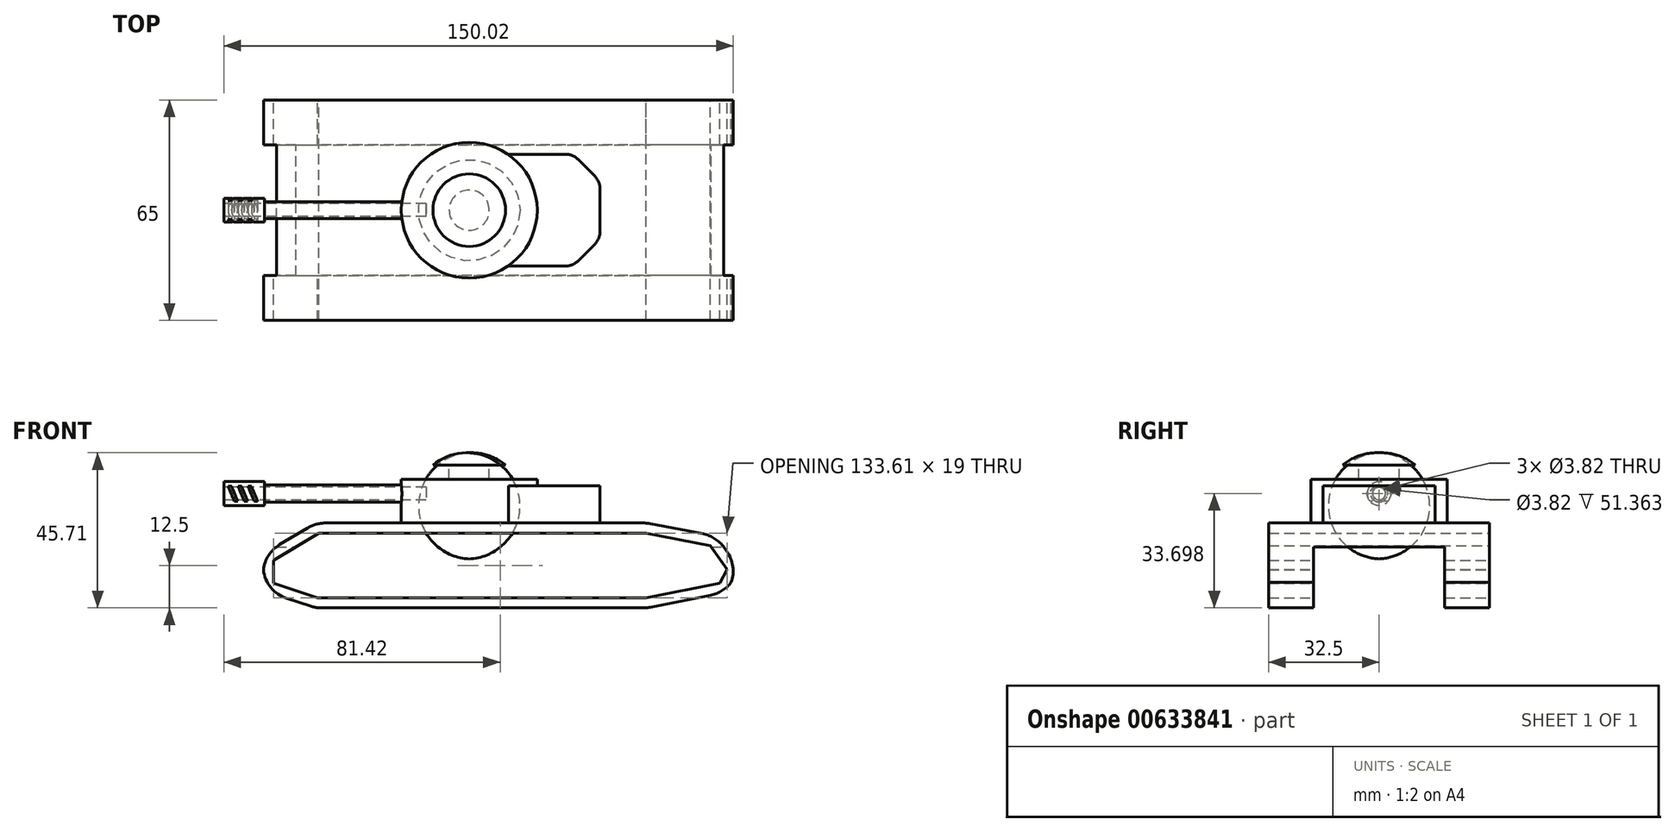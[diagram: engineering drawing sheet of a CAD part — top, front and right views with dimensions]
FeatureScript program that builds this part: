
annotation { "Feature Type Name" : "Feature", "Feature Type Description" : "" }
export const myFeature = defineFeature(function(context is Context, id is Id, definition is map)
    precondition{}
    {
        {
            var Q0;
            Q0=qCreatedBy(makeId("Front.planeOp"),FACE);
            var sketch = newSketch(context, id + "F0", { "sketchPlane" : qUnion([Q0])});
            skLineSegment(sketch, "E0.bottom", {"start": v(0, 0) * mm, "end": v(52.39, 0) * mm});
            skLineSegment(sketch, "E0.top", {"start": v(0, 25) * mm, "end": v(52.39, 25) * mm});
            skLineSegment(sketch, "E1.bottom", {"start": v(0, 25) * mm, "end": v(-45.2, 25) * mm});
            skLineSegment(sketch, "E1.top", {"start": v(0, 0) * mm, "end": v(-45.2, 0) * mm});
            skLineSegment(sketch, "E2", {"start": v(-45.2, 25) * mm, "end": v(-60.69, 15.75) * mm});
            skLineSegment(sketch, "E3", {"start": v(-60.69, 15.75) * mm, "end": v(-60.69, 5.11) * mm});
            skLineSegment(sketch, "E4", {"start": v(-60.69, 5.11) * mm, "end": v(-45.2, 0) * mm});
            skLineSegment(sketch, "E5", {"start": v(52.39, 25) * mm, "end": v(72.74, 21.07) * mm});
            skLineSegment(sketch, "E6", {"start": v(72.74, 21.07) * mm, "end": v(79.44, 11.59) * mm});
            skLineSegment(sketch, "E7", {"start": v(79.44, 11.59) * mm, "end": v(75.74, 4.65) * mm});
            skLineSegment(sketch, "E8", {"start": v(75.74, 4.65) * mm, "end": v(52.39, 0) * mm});
            skLineSegment(sketch, "E9.bottom", {"start": v(20.02, 37.95) * mm, "end": v(-20.02, 37.95) * mm});
            skLineSegment(sketch, "E9.left", {"start": v(20.02, 37.95) * mm, "end": v(20.02, 25) * mm});
            skLineSegment(sketch, "E9.right", {"start": v(-20.02, 37.95) * mm, "end": v(-20.02, 25) * mm});
            skPoint(sketch, "E9.middle", {"position": v(0, 25) * mm});
            skLineSegment(sketch, "E10", {"start": v(0, 37.95) * mm, "end": v(0, 25) * mm});
            skLineSegment(sketch, "E11.bottom", {"start": v(5.91, 42.11) * mm, "end": v(-5.91, 42.11) * mm});
            skLineSegment(sketch, "E11.top", {"start": v(5.91, 33.79) * mm, "end": v(-5.91, 33.79) * mm});
            skLineSegment(sketch, "E11.left", {"start": v(5.91, 42.11) * mm, "end": v(5.91, 33.79) * mm});
            skLineSegment(sketch, "E11.right", {"start": v(-5.91, 42.11) * mm, "end": v(-5.91, 33.79) * mm});
            skPoint(sketch, "E11.middle", {"position": v(0, 37.95) * mm});
            skArc(sketch, "E12", {"start": v(10.7, 42.11) * mm, "mid": v(5.68, 44.9) * mm, "end": v(0, 45.7) * mm});
            skLineSegment(sketch, "E13", {"start": v(5.91, 42.11) * mm, "end": v(10.7, 42.11) * mm});
            skLineSegment(sketch, "E14", {"start": v(0, 42.11) * mm, "end": v(0, 45.94) * mm});
            skPoint(sketch, "E14.endSnap0", {"position": v(0, 42.11) * mm});
            skLineSegment(sketch, "E15", {"start": v(0, 42.11) * mm, "end": v(0, 37.95) * mm});
            skSolve(sketch);
        }
        {
            var Q0;
            Q0=makeQuery(id+"F0.imprint","IMPRINT",FACE,{"disambiguationData":[TD([[makeQuery(id+"F0.imprint","IMPRINT",EDGE,{"derivedFrom":sQuery(id+"F0.wireOp",EDGE,"E0.bottom")}),1.0]])]});
            extrude(context, id + "F1", {"entities" : qUnion([Q0]), "endBound" : BoundingType.SYMMETRIC, "depth" : 65 * mm, "offsetDistance" : 25 * mm});
        }
        {
            var Q0;
            {var subQ5=sQuery(id+"F0.wireOp",EDGE,"E9.left");Q0=makeQuery(id+"F0.imprint","IMPRINT",FACE,{"disambiguationData":[TD([[makeQuery(id+"F0.imprint","IMPRINT",EDGE,{"derivedFrom":subQ5}),-1.0]])]});}
            var Q1;
            {var subQ0=sQuery(id+"F0.wireOp",EDGE,"E10");var subQ1=sQuery(id+"F0.wireOp",EDGE,"E9.bottom");var subQ2=makeQuery(id+"F0.imprint","INTERSECT",VERTEX,{"derivedFrom":[subQ1,subQ0]});Q1=makeQuery(id+"F0.imprint","IMPRINT",FACE,{"disambiguationData":[TD([[makeQuery(id+"F0.imprint","IMPRINT",EDGE,{"disambiguationData":[TD([[subQ2,1.0]])],"derivedFrom":subQ1}),1.0]])]});}
            var Q2;
            Q2=sQuery(id+"F0.wireOp",EDGE,"E10");
            revolve(context, id + "F2", {"operationType" : NewBodyOperationType.ADD, "entities" : qUnion([Q0, Q1]), "axis" : qUnion([Q2]), "revolveType" : RevolveType.FULL});
        }
        {
            var Q0;
            {var subQ0=sQuery(id+"F0.wireOp",EDGE,"E15");Q0=makeQuery(id+"F0.imprint","IMPRINT",FACE,{"disambiguationData":[TD([[makeQuery(id+"F0.imprint","IMPRINT",EDGE,{"derivedFrom":subQ0}),1.0]])]});}
            var Q1;
            Q1=sQuery(id+"F0.wireOp",EDGE,"E15");
            revolve(context, id + "F3", {"operationType" : NewBodyOperationType.ADD, "entities" : qUnion([Q0]), "axis" : qUnion([Q1]), "revolveType" : RevolveType.FULL});
        }
        {
            var Q0;
            {var subQ4=sQuery(id+"F0.wireOp",EDGE,"E12");Q0=makeQuery(id+"F0.imprint","IMPRINT",FACE,{"disambiguationData":[TD([[makeQuery(id+"F0.imprint","IMPRINT",EDGE,{"derivedFrom":subQ4}),1.0]])]});}
            var Q1;
            Q1=sQuery(id+"F0.wireOp",EDGE,"E14");
            revolve(context, id + "F4", {"operationType" : NewBodyOperationType.ADD, "entities" : qUnion([Q0]), "axis" : qUnion([Q1]), "revolveType" : RevolveType.FULL});
        }
        {
            var Q0;
            Q0=qCreatedBy(makeId("Right.planeOp"),FACE);
            var sketch = newSketch(context, id + "F5", { "sketchPlane" : qUnion([Q0])});
            skCircle(sketch, "E16", {"center": v(0, 33.7) * mm, "radius": 2.5 * mm});
            skSolve(sketch);
        }
        {
            var Q0;
            Q0 = qSketchRegion(id + "F5", true);
            extrude(context, id + "F6", {"entities" : qUnion([Q0]), "operationType" : NewBodyOperationType.ADD, "oppositeDirection" : true, "depth" : 65.3 * mm, "offsetDistance" : 25 * mm});
        }
        {
            var Q0;
            Q0=makeQuery(id+"F6.opExtrude","CAP_FACE",FACE,{"disambiguationData":[OSD([sQuery(id+"F5.wireOp",EDGE,"E16")])],"isStart":false});
            cPlane(context, id + "F7", {"entities" : qUnion([Q0]), "cplaneType" : CPlaneType.OFFSET, "offset" : 7 * mm, "width" : 150 * mm, "height" : 150 * mm});
        }
        {
            var Q0;
            Q0=qCreatedBy(id+"F7.planeOp",FACE);
            var sketch = newSketch(context, id + "F8", { "sketchPlane" : qUnion([Q0])});
            skPoint(sketch, "E17", {"position": v(0, 33.7) * mm});
            skCircle(sketch, "E18", {"center": v(0, 33.7) * mm, "radius": 3.5 * mm});
            skLineSegment(sketch, "E19", {"start": v(0, 33.7) * mm, "end": v(0, 30.85) * mm, "construction": true});
            skCircle(sketch, "E20", {"center": v(0, 33.7) * mm, "radius": 1.9 * mm});
            skSolve(sketch);
        }
        {
            var Q0;
            Q0=makeQuery(id+"F8.imprint","IMPRINT",FACE,{"disambiguationData":[TD([[makeQuery(id+"F8.imprint","IMPRINT",EDGE,{"derivedFrom":sQuery(id+"F8.wireOp",EDGE,"E18")}),1.0]])]});
            extrude(context, id + "F9", {"entities" : qUnion([Q0]), "operationType" : NewBodyOperationType.ADD, "oppositeDirection" : true, "depth" : 12 * mm, "offsetDistance" : 25 * mm});
        }
        {
            var Q0;
            Q0=qCreatedBy(id+"F7.planeOp",FACE);
            var Q1;
            Q1=sQuery(id+"F8.wireOp",EDGE,"E19");
            cPlane(context, id + "F10", {"entities" : qUnion([Q0, Q1]), "cplaneType" : CPlaneType.LINE_ANGLE, "offset" : 25 * mm, "angle" : 90 * degree, "width" : 150 * mm, "height" : 150 * mm});
        }
        {
            var Q0;
            Q0=qCreatedBy(id+"F10.planeOp",FACE);
            var sketch = newSketch(context, id + "F11", { "sketchPlane" : qUnion([Q0])});
            skLineSegment(sketch, "E21", {"start": v(-70, 35.81) * mm, "end": v(-68.2, 31.44) * mm});
            skLineSegment(sketch, "E22", {"start": v(-71, 35.81) * mm, "end": v(-69.2, 31.44) * mm});
            skLineSegment(sketch, "E23", {"start": v(-70, 35.81) * mm, "end": v(-71, 35.81) * mm});
            skLineSegment(sketch, "E24", {"start": v(-68.2, 31.44) * mm, "end": v(-69.2, 31.44) * mm});
            skLineSegment(sketch, "E25.1.0.0", {"start": v(-67.07, 35.81) * mm, "end": v(-65.27, 31.44) * mm});
            skLineSegment(sketch, "E25.1.0.1", {"start": v(-67.07, 35.81) * mm, "end": v(-68.08, 35.81) * mm});
            skLineSegment(sketch, "E25.1.0.2", {"start": v(-68.08, 35.81) * mm, "end": v(-66.28, 31.44) * mm});
            skLineSegment(sketch, "E25.1.0.3", {"start": v(-65.27, 31.44) * mm, "end": v(-66.28, 31.44) * mm});
            skLineSegment(sketch, "E25.2.0.0", {"start": v(-64.15, 35.81) * mm, "end": v(-62.34, 31.44) * mm});
            skLineSegment(sketch, "E25.2.0.1", {"start": v(-64.15, 35.81) * mm, "end": v(-65.15, 35.81) * mm});
            skLineSegment(sketch, "E25.2.0.2", {"start": v(-65.15, 35.81) * mm, "end": v(-63.35, 31.44) * mm});
            skLineSegment(sketch, "E25.2.0.3", {"start": v(-62.34, 31.44) * mm, "end": v(-63.35, 31.44) * mm});
            skLineSegment(sketch, "E25.direction1", {"start": v(-68.2, 31.44) * mm, "end": v(-65.27, 31.44) * mm, "construction": true});
            skSolve(sketch);
        }
        {
            var Q0;
            Q0 = qSketchRegion(id + "F11", true);
            extrude(context, id + "F12", {"entities" : qUnion([Q0]), "operationType" : NewBodyOperationType.REMOVE, "endBound" : BoundingType.SYMMETRIC, "oppositeDirection" : true, "depth" : 25 * mm, "offsetDistance" : 25 * mm});
        }
        {
            var Q0;
            Q0=makeQuery(id+"F8.imprint","IMPRINT",FACE,{"disambiguationData":[TD([[makeQuery(id+"F8.imprint","IMPRINT",EDGE,{"derivedFrom":sQuery(id+"F8.wireOp",EDGE,"E20")}),1.0]])]});
            extrude(context, id + "F13", {"entities" : qUnion([Q0]), "operationType" : NewBodyOperationType.REMOVE, "oppositeDirection" : true, "depth" : 59.6 * mm, "offsetDistance" : 25 * mm});
        }
        {
            var Q0;
            Q0=makeQuery(id+"F1.opExtrude","SWEPT_EDGE",EDGE,{"disambiguationData":[OSD([sQuery(id+"F0.wireOp",EDGE,"E1.bottom"),sQuery(id+"F0.wireOp",EDGE,"E2")])]});
            var Q1;
            Q1=makeQuery(id+"F1.opExtrude","SWEPT_EDGE",EDGE,{"disambiguationData":[OSD([sQuery(id+"F0.wireOp",EDGE,"E2"),sQuery(id+"F0.wireOp",EDGE,"E3")])]});
            var Q2;
            Q2=makeQuery(id+"F1.opExtrude","SWEPT_EDGE",EDGE,{"disambiguationData":[OSD([sQuery(id+"F0.wireOp",EDGE,"E3"),sQuery(id+"F0.wireOp",EDGE,"E4")])]});
            var Q3;
            Q3=makeQuery(id+"F1.opExtrude","SWEPT_EDGE",EDGE,{"disambiguationData":[OSD([sQuery(id+"F0.wireOp",EDGE,"E1.top"),sQuery(id+"F0.wireOp",EDGE,"E4")])]});
            var Q4;
            Q4=makeQuery(id+"F1.opExtrude","SWEPT_EDGE",EDGE,{"disambiguationData":[OSD([sQuery(id+"F0.wireOp",EDGE,"E0.bottom"),sQuery(id+"F0.wireOp",EDGE,"E8")])]});
            var Q5;
            Q5=makeQuery(id+"F1.opExtrude","SWEPT_EDGE",EDGE,{"disambiguationData":[OSD([sQuery(id+"F0.wireOp",EDGE,"E7"),sQuery(id+"F0.wireOp",EDGE,"E8")])]});
            var Q6;
            Q6=makeQuery(id+"F1.opExtrude","SWEPT_EDGE",EDGE,{"disambiguationData":[OSD([sQuery(id+"F0.wireOp",EDGE,"E6"),sQuery(id+"F0.wireOp",EDGE,"E7")])]});
            var Q7;
            Q7=makeQuery(id+"F1.opExtrude","SWEPT_EDGE",EDGE,{"disambiguationData":[OSD([sQuery(id+"F0.wireOp",EDGE,"E5"),sQuery(id+"F0.wireOp",EDGE,"E6")])]});
            var Q8;
            Q8=makeQuery(id+"F1.opExtrude","SWEPT_EDGE",EDGE,{"disambiguationData":[OSD([sQuery(id+"F0.wireOp",EDGE,"E0.top"),sQuery(id+"F0.wireOp",EDGE,"E5")])]});
            fillet(context, id + "F14", {"entities" : qUnion([Q0, Q1, Q2, Q3, Q4, Q5, Q6, Q7, Q8]), "radius" : 10 * mm, "tangentPropagation" : true, "allowEdgeOverflow" : false});
        }
        {
            var Q0;
            Q0=makeQuery(id+"F1.opExtrude","CAP_FACE",FACE,{"disambiguationData":[OSD([sQuery(id+"F0.wireOp",EDGE,"E0.bottom"),sQuery(id+"F0.wireOp",EDGE,"E0.top"),sQuery(id+"F0.wireOp",EDGE,"E1.bottom"),sQuery(id+"F0.wireOp",EDGE,"E1.top"),sQuery(id+"F0.wireOp",EDGE,"E2"),sQuery(id+"F0.wireOp",EDGE,"E3"),sQuery(id+"F0.wireOp",EDGE,"E4"),sQuery(id+"F0.wireOp",EDGE,"E5"),sQuery(id+"F0.wireOp",EDGE,"E6"),sQuery(id+"F0.wireOp",EDGE,"E7"),sQuery(id+"F0.wireOp",EDGE,"E8")])],"isStart":true});
            var sketch = newSketch(context, id + "F15", { "sketchPlane" : qUnion([Q0])});
            skLineSegment(sketch, "E26.0", {"start": v(-73.77, 7.32) * mm, "end": v(-52.1, 3) * mm});
            skLineSegment(sketch, "E26.1", {"start": v(-75.93, 11.37) * mm, "end": v(-73.77, 7.32) * mm});
            skLineSegment(sketch, "E26.2", {"start": v(-70.98, 18.35) * mm, "end": v(-75.93, 11.37) * mm});
            skLineSegment(sketch, "E26.3", {"start": v(-52.1, 22) * mm, "end": v(-70.98, 18.35) * mm});
            skLineSegment(sketch, "E26.4", {"start": v(0, 22) * mm, "end": v(-52.1, 22) * mm});
            skLineSegment(sketch, "E26.5", {"start": v(0, 3) * mm, "end": v(-52.1, 3) * mm});
            skLineSegment(sketch, "E26.6", {"start": v(0, 3) * mm, "end": v(44.71, 3) * mm});
            skLineSegment(sketch, "E26.7", {"start": v(57.69, 7.28) * mm, "end": v(44.71, 3) * mm});
            skLineSegment(sketch, "E26.8", {"start": v(57.69, 14.05) * mm, "end": v(57.69, 7.28) * mm});
            skLineSegment(sketch, "E26.9", {"start": v(44.37, 22) * mm, "end": v(57.69, 14.05) * mm});
            skLineSegment(sketch, "E26.10", {"start": v(0, 22) * mm, "end": v(44.37, 22) * mm});
            skSolve(sketch);
        }
        {
            var Q0;
            Q0=makeQuery(id+"F15.imprint","IMPRINT",FACE,{"disambiguationData":[TD([[makeQuery(id+"F15.imprint","IMPRINT",EDGE,{"derivedFrom":sQuery(id+"F15.wireOp",EDGE,"E26.0")}),1.0]])]});
            extrude(context, id + "F16", {"entities" : qUnion([Q0]), "operationType" : NewBodyOperationType.REMOVE, "endBound" : BoundingType.THROUGH_ALL, "oppositeDirection" : true, "depth" : 25 * mm, "offsetDistance" : 25 * mm});
        }
        {
            var Q0;
            Q0=qCreatedBy(makeId("Right.planeOp"),FACE);
            var sketch = newSketch(context, id + "F17", { "sketchPlane" : qUnion([Q0])});
            skLineSegment(sketch, "E27.bottom", {"start": v(-19.29, 18) * mm, "end": v(19.29, 18) * mm});
            skLineSegment(sketch, "E27.top", {"start": v(-19.29, -18) * mm, "end": v(19.29, -18) * mm});
            skLineSegment(sketch, "E27.left", {"start": v(-19.29, 18) * mm, "end": v(-19.29, -18) * mm});
            skLineSegment(sketch, "E27.right", {"start": v(19.29, 18) * mm, "end": v(19.29, -18) * mm});
            skPoint(sketch, "E27.middle", {"position": v(0, 0) * mm});
            skSolve(sketch);
        }
        {
            var Q0;
            Q0=makeQuery(id+"F17.imprint","IMPRINT",FACE,{"disambiguationData":[TD([[makeQuery(id+"F17.imprint","IMPRINT",EDGE,{"derivedFrom":sQuery(id+"F17.wireOp",EDGE,"E27.bottom")}),-1.0]])]});
            extrude(context, id + "F18", {"entities" : qUnion([Q0]), "operationType" : NewBodyOperationType.REMOVE, "endBound" : BoundingType.SYMMETRIC, "oppositeDirection" : true, "depth" : 160 * mm, "offsetDistance" : 25 * mm});
        }
        {
            var Q0;
            Q0=qCreatedBy(makeId("Right.planeOp"),FACE);
            cPlane(context, id + "F19", {"entities" : qUnion([Q0]), "cplaneType" : CPlaneType.OFFSET, "offset" : 25 * mm, "width" : 150 * mm, "height" : 150 * mm});
        }
        {
            var Q0;
            Q0=qCreatedBy(id+"F19.planeOp",FACE);
            var sketch = newSketch(context, id + "F20", { "sketchPlane" : qUnion([Q0])});
            skPoint(sketch, "E28", {"position": v(0, 25) * mm});
            skLineSegment(sketch, "E29.bottom", {"start": v(0, 25) * mm, "end": v(16.47, 25) * mm});
            skLineSegment(sketch, "E29.top", {"start": v(0, 36) * mm, "end": v(16.47, 36) * mm});
            skLineSegment(sketch, "E29.right", {"start": v(16.47, 25) * mm, "end": v(16.47, 36) * mm});
            skLineSegment(sketch, "E30.MirrorCS", {"start": v(0, 36) * mm, "end": v(-16.47, 36) * mm});
            skLineSegment(sketch, "E31.MirrorCS", {"start": v(-16.47, 25) * mm, "end": v(-16.47, 36) * mm});
            skLineSegment(sketch, "E32.MirrorCS", {"start": v(0, 25) * mm, "end": v(-16.47, 25) * mm});
            skSolve(sketch);
        }
        {
            var Q0;
            Q0 = qSketchRegion(id + "F20", true);
            extrude(context, id + "F21", {"entities" : qUnion([Q0]), "operationType" : NewBodyOperationType.ADD, "endBound" : BoundingType.SYMMETRIC, "depth" : 27 * mm, "offsetDistance" : 25 * mm});
        }
        {
            var Q0;
            Q0=makeQuery(id+"F21.opExtrude","CAP_EDGE",EDGE,{"disambiguationData":[OSD([sQuery(id+"F20.wireOp",EDGE,"E29.right")])],"isStart":false});
            var Q1;
            Q1=makeQuery(id+"F21.opExtrude","CAP_EDGE",EDGE,{"disambiguationData":[OSD([sQuery(id+"F20.wireOp",EDGE,"E31.MirrorCS")])],"isStart":false});
            chamfer(context, id + "F22", {"entities" : qUnion([Q0, Q1]), "width" : 8 * mm, "tangentPropagation" : true});
        }
        {
            var Q0;
            {var subQ0=sQuery(id+"F20.wireOp",EDGE,"E31.MirrorCS");Q0=makeQuery(id+"F22.opChamfer","BLEND_EDGE",EDGE,{"blendedFrom":[makeQuery(id+"F21.opExtrude","CAP_EDGE",EDGE,{"disambiguationData":[OSD([subQ0])],"isStart":false}),makeQuery(id+"F21.opExtrude","CAP_FACE",FACE,{"disambiguationData":[OSD([sQuery(id+"F20.wireOp",EDGE,"E29.bottom"),sQuery(id+"F20.wireOp",EDGE,"E29.top"),sQuery(id+"F20.wireOp",EDGE,"E29.right"),sQuery(id+"F20.wireOp",EDGE,"E30.MirrorCS"),subQ0,sQuery(id+"F20.wireOp",EDGE,"E32.MirrorCS")])],"isStart":false})],"blendedInto":[makeQuery(id+"F21.opExtrude","CAP_FACE",FACE,{"disambiguationData":[OSD([sQuery(id+"F20.wireOp",EDGE,"E29.bottom"),sQuery(id+"F20.wireOp",EDGE,"E29.top"),sQuery(id+"F20.wireOp",EDGE,"E29.right"),sQuery(id+"F20.wireOp",EDGE,"E30.MirrorCS"),subQ0,sQuery(id+"F20.wireOp",EDGE,"E32.MirrorCS")])],"isStart":false})]});}
            var Q1;
            {var subQ0=sQuery(id+"F20.wireOp",EDGE,"E31.MirrorCS");Q1=makeQuery(id+"F22.opChamfer","BLEND_EDGE",EDGE,{"blendedFrom":[makeQuery(id+"F21.opExtrude","CAP_EDGE",EDGE,{"disambiguationData":[OSD([subQ0])],"isStart":false}),makeQuery(id+"F21.opExtrude","SWEPT_FACE",FACE,{"disambiguationData":[OSD([subQ0])]})],"blendedInto":[makeQuery(id+"F21.opExtrude","SWEPT_FACE",FACE,{"disambiguationData":[OSD([subQ0])]})]});}
            var Q2;
            {var subQ0=sQuery(id+"F20.wireOp",EDGE,"E29.right");Q2=makeQuery(id+"F22.opChamfer","BLEND_EDGE",EDGE,{"blendedFrom":[makeQuery(id+"F21.opExtrude","CAP_EDGE",EDGE,{"disambiguationData":[OSD([subQ0])],"isStart":false}),makeQuery(id+"F21.opExtrude","CAP_FACE",FACE,{"disambiguationData":[OSD([sQuery(id+"F20.wireOp",EDGE,"E29.bottom"),sQuery(id+"F20.wireOp",EDGE,"E29.top"),subQ0,sQuery(id+"F20.wireOp",EDGE,"E30.MirrorCS"),sQuery(id+"F20.wireOp",EDGE,"E31.MirrorCS"),sQuery(id+"F20.wireOp",EDGE,"E32.MirrorCS")])],"isStart":false})],"blendedInto":[makeQuery(id+"F21.opExtrude","CAP_FACE",FACE,{"disambiguationData":[OSD([sQuery(id+"F20.wireOp",EDGE,"E29.bottom"),sQuery(id+"F20.wireOp",EDGE,"E29.top"),subQ0,sQuery(id+"F20.wireOp",EDGE,"E30.MirrorCS"),sQuery(id+"F20.wireOp",EDGE,"E31.MirrorCS"),sQuery(id+"F20.wireOp",EDGE,"E32.MirrorCS")])],"isStart":false})]});}
            var Q3;
            {var subQ0=sQuery(id+"F20.wireOp",EDGE,"E29.right");Q3=makeQuery(id+"F22.opChamfer","BLEND_EDGE",EDGE,{"blendedFrom":[makeQuery(id+"F21.opExtrude","CAP_EDGE",EDGE,{"disambiguationData":[OSD([subQ0])],"isStart":false}),makeQuery(id+"F21.opExtrude","SWEPT_FACE",FACE,{"disambiguationData":[OSD([subQ0])]})],"blendedInto":[makeQuery(id+"F21.opExtrude","SWEPT_FACE",FACE,{"disambiguationData":[OSD([subQ0])]})]});}
            fillet(context, id + "F23", {"entities" : qUnion([Q0, Q1, Q2, Q3]), "radius" : 5 * mm, "tangentPropagation" : true, "allowEdgeOverflow" : false});
        }
    });
